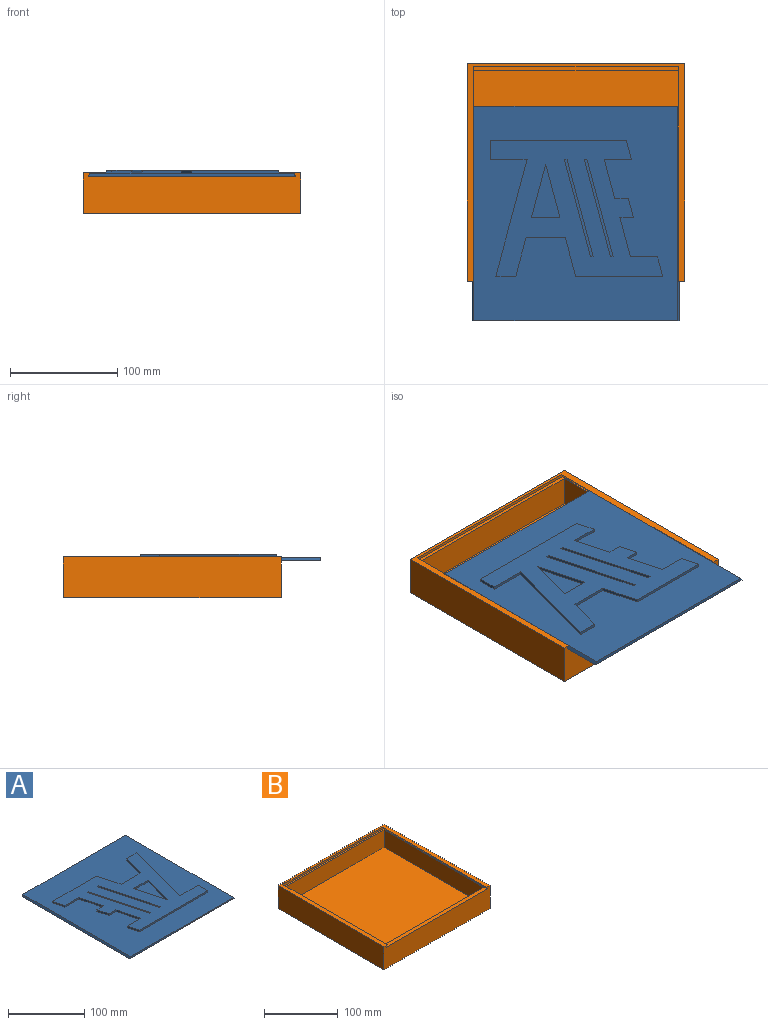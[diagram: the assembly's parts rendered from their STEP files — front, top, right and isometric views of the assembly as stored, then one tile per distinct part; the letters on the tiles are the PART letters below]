
ASSEMBLY  parts=2 mates=2
PART A: 40 faces, bbox 193.6x200x5.5 mm
  f0: plane 200.03x190.25mm, normal (0,0,1), area 25670.8mm2, adj f1,f3,f4,f5,f15,f16,f17,f18
  f1: plane 200.03x2.92mm, normal (-0.87,0,0.5), area 674.3mm2, adj f0,f2,f4,f5,f6
  f2: plane 199.26x193.62mm, normal (0,0,-1), area 38581.1mm2, adj f1,f3,f5,f6
  f3: plane 200.03x2.92mm, normal (0.87,0,0.5), area 674.3mm2, adj f0,f2,f4,f5,f6
  f4: plane 192.74x2.16mm, normal (0,-1,0), area 413.4mm2, adj f0,f1,f3,f6
  f5: plane 193.62x2.92mm, normal (0,1,0), area 560.6mm2, adj f0,f1,f2,f3
  f6: plane 193.62x0.76mm, normal (0,-0.71,-0.71), area 208.2mm2, adj f1,f2,f3,f4
  f7: plane 2.54x2.54mm, normal (0,-1,0), area 6.5mm2, adj f8,f35,f36,f37
  f8: plane 91.02x24.39mm, normal (-0.97,-0.26,0), area 239.3mm2, adj f7,f9,f36,f37
  f9: plane 2.54x2.54mm, normal (0,1,0), area 6.5mm2, adj f8,f35,f36,f37
  f10: plane 26.67x2.54mm, normal (0,-1,0), area 67.7mm2, adj f11,f32,f36,f38
  f11: plane 49.77x13.34mm, normal (-0.97,0.26,0), area 130.9mm2, adj f10,f32,f36,f38
  f12: plane 91.02x24.39mm, normal (-0.97,-0.26,0), area 239.3mm2, adj f13,f33,f36,f39
  f13: plane 2.54x2.54mm, normal (0,1,0), area 6.5mm2, adj f12,f14,f36,f39
  f14: plane 91.02x24.39mm, normal (0.97,0.26,0), area 239.3mm2, adj f13,f33,f36,f39
  f15: plane 127x2.54mm, normal (0,-1,0), area 322.6mm2, adj f0,f16,f34,f36
  f16: plane 17.99x2.54mm, normal (1,0,0), area 45.7mm2, adj f0,f15,f17,f36
  f17: plane 34.45x2.54mm, normal (0,1,0), area 87.5mm2, adj f0,f16,f18,f36
  f18: plane 109.01x29.21mm, normal (0.97,-0.26,0), area 286.6mm2, adj f0,f17,f19,f36
  f19: plane 18.63x2.54mm, normal (0,1,0), area 47.3mm2, adj f0,f18,f20,f36
  f20: plane 35.88x9.61mm, normal (-0.97,0.26,0), area 94.3mm2, adj f0,f19,f21,f36
  f21: plane 36.65x2.54mm, normal (0,1,0), area 93.1mm2, adj f0,f20,f22,f36
  f22: plane 35.88x9.61mm, normal (0.97,0.26,0), area 94.3mm2, adj f0,f21,f23,f36
  f23: plane 81.28x2.54mm, normal (0,1,0), area 206.5mm2, adj f0,f22,f24,f36
  f24: plane 17.99x4.82mm, normal (-0.97,-0.26,0), area 47.3mm2, adj f0,f23,f25,f36
  f25: plane 25.4x2.54mm, normal (0,-1,0), area 64.5mm2, adj f0,f24,f26,f36
  f26: plane 36.51x9.78mm, normal (-0.97,-0.26,0), area 96mm2, adj f0,f25,f27,f36
  f27: plane 12.7x2.54mm, normal (0,1,0), area 32.3mm2, adj f0,f26,f28,f36
  f28: plane 17.99x4.82mm, normal (-0.97,-0.26,0), area 47.3mm2, adj f0,f27,f29,f36
  f29: plane 12.7x2.54mm, normal (0,-1,0), area 32.3mm2, adj f0,f28,f30,f36
  f30: plane 36.51x9.78mm, normal (-0.97,-0.26,0), area 96mm2, adj f0,f29,f31,f36
  f31: plane 25.4x2.54mm, normal (0,1,0), area 64.5mm2, adj f0,f30,f34,f36
  f32: plane 49.77x13.34mm, normal (0.97,0.26,0), area 130.9mm2, adj f10,f11,f36,f38
  f33: plane 2.54x2.54mm, normal (0,-1,0), area 6.5mm2, adj f12,f14,f36,f39
  f34: plane 17.99x4.82mm, normal (-0.97,-0.26,0), area 47.3mm2, adj f0,f15,f31,f36
  f35: plane 91.02x24.39mm, normal (0.97,0.26,0), area 239.3mm2, adj f7,f9,f36,f37
  f36: plane 161.03x127mm, normal (0,0,1), area 11257.1mm2, adj f7,f8,f9,f10,f11,f12,f13,f14
  f37: plane 91.02x26.93mm, normal (0,0,1), area 231.2mm2, adj f7,f8,f9,f35
  f38: plane 49.77x26.67mm, normal (0,0,1), area 663.7mm2, adj f10,f11,f32
  f39: plane 91.02x26.93mm, normal (0,0,1), area 231.2mm2, adj f12,f13,f14,f33
PART B: 15 faces, bbox 203.2x203.2x38.1 mm
  f0: plane 203.2x203.2mm, normal (0,0,1), area 3185.5mm2, adj f1,f2,f3,f4,f7,f8,f9
  f1: plane 203.2x38.1mm, normal (0,-1,0), area 7155.9mm2, adj f0,f2,f4,f5,f6,f7,f8
  f2: plane 203.2x38.1mm, normal (1,0,0), area 7741.9mm2, adj f0,f1,f3,f5
  f3: plane 203.2x38.1mm, normal (0,1,0), area 7741.9mm2, adj f0,f2,f4,f5
  f4: plane 203.2x38.1mm, normal (-1,0,0), area 7741.9mm2, adj f0,f1,f3,f5
  f5: plane 203.2x203.2mm, normal (0,0,-1), area 41290.2mm2, adj f1,f2,f3,f4
  f6: plane 200.03x194.02mm, normal (0,0,1), area 2518.5mm2, adj f1,f7,f8,f9,f11,f12,f13,f14
  f7: plane 200.03x3.05mm, normal (-0.87,0,-0.5), area 704mm2, adj f0,f1,f6,f9
  f8: plane 200.03x3.05mm, normal (0.87,0,-0.5), area 704mm2, adj f0,f1,f6,f9
  f9: plane 194.02x3.05mm, normal (0,-1,0), area 586mm2, adj f0,f6,f7,f8
  f10: plane 190.5x190.5mm, normal (0,0,1), area 36290.2mm2, adj f11,f12,f13,f14
  f11: plane 190.5x28.7mm, normal (0,-1,0), area 5467.7mm2, adj f6,f10,f12,f14
  f12: plane 190.5x28.7mm, normal (-1,0,0), area 5467.7mm2, adj f6,f10,f11,f13
  f13: plane 190.5x28.7mm, normal (0,1,0), area 5467.7mm2, adj f6,f10,f12,f14
  f14: plane 190.5x28.7mm, normal (1,0,0), area 5467.7mm2, adj f6,f10,f11,f13
PLACE A rot(axis=(0,0,-1),180deg) t=(-32.71,-194.21,79.95)mm
PLACE B t=(-32.51,-56.04,44.9)mm fixed
MATE planar B.f8 <-> A.f3  axis (0.87,0,-0.5) through (-128.64,-57.62,81.47)mm
MATE planar B.f6 <-> A.f2  axis (0,0,1) through (-32.51,-80.5,79.95)mm
